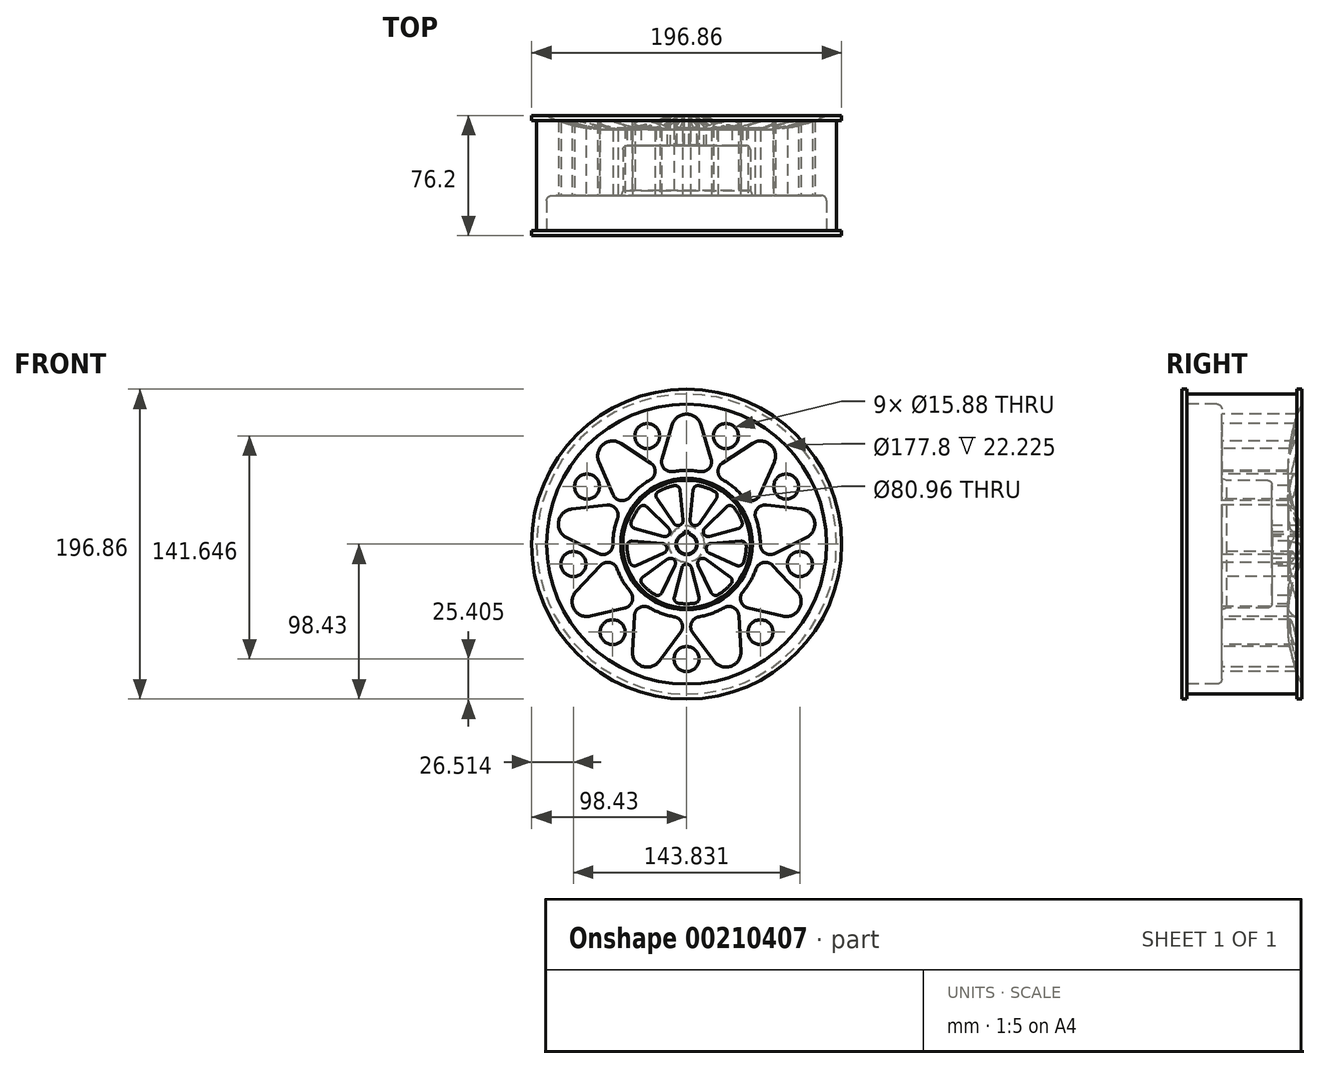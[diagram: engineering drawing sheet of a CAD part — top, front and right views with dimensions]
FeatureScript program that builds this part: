
annotation { "Feature Type Name" : "Feature", "Feature Type Description" : "" }
export const myFeature = defineFeature(function(context is Context, id is Id, definition is map)
    precondition{}
    {
        {
            var Q0;
            Q0=qCreatedBy(makeId("Right.planeOp"),FACE);
            var sketch = newSketch(context, id + "F0", { "sketchPlane" : qUnion([Q0])});
            skLineSegment(sketch, "E0.bottom", {"start": v(-34.93, 95.25) * mm, "end": v(34.92, 95.25) * mm});
            skLineSegment(sketch, "E0.top", {"start": v(19.05, 6.35) * mm, "end": v(38.1, 6.35) * mm});
            skLineSegment(sketch, "E1", {"start": v(38.1, 98.43) * mm, "end": v(34.92, 98.43) * mm});
            skLineSegment(sketch, "E2", {"start": v(34.92, 98.43) * mm, "end": v(34.92, 95.25) * mm});
            skLineSegment(sketch, "E3", {"start": v(38.1, 6.35) * mm, "end": v(38.1, 11.43) * mm});
            skLineSegment(sketch, "E4", {"start": v(-38.1, 88.9) * mm, "end": v(-38.1, 98.43) * mm});
            skLineSegment(sketch, "E5", {"start": v(-38.1, 98.43) * mm, "end": v(-34.93, 98.43) * mm});
            skLineSegment(sketch, "E6", {"start": v(-34.93, 98.43) * mm, "end": v(-34.93, 95.25) * mm});
            skLineSegment(sketch, "E7", {"start": v(-79.55, 0) * mm, "end": v(86.59, 0) * mm, "construction": true});
            skLineSegment(sketch, "E8", {"start": v(19.05, 6.35) * mm, "end": v(19.05, 37.94) * mm});
            skLineSegment(sketch, "E9", {"start": v(-15.88, 88.9) * mm, "end": v(-38.1, 88.9) * mm});
            skLineSegment(sketch, "E10", {"start": v(16.51, 40.48) * mm, "end": v(-12.7, 40.48) * mm});
            skLineSegment(sketch, "E11", {"start": v(-12.7, 40.48) * mm, "end": v(-12.7, 85.73) * mm});
            skPoint(sketch, "E12", {"position": v(38.1, 88.9) * mm});
            skPoint(sketch, "E13", {"position": v(38.1, 11.43) * mm});
            skArc(sketch, "E14", {"start": v(38.1, 88.9) * mm, "mid": v(29.22, 50.16) * mm, "end": v(38.1, 11.43) * mm});
            skLineSegment(sketch, "E15.trimOffspring", {"start": v(38.1, 88.9) * mm, "end": v(38.1, 98.43) * mm});
            skPoint(sketch, "E16.visualSharp", {"position": v(19.05, 40.48) * mm});
            skArc(sketch, "E16.filletArc", {"start": v(19.05, 37.94) * mm, "mid": v(18.3, 39.74) * mm, "end": v(16.51, 40.48) * mm});
            skPoint(sketch, "E17.visualSharp", {"position": v(-12.7, 88.9) * mm});
            skArc(sketch, "E17.filletArc", {"start": v(-12.7, 85.73) * mm, "mid": v(-13.63, 87.97) * mm, "end": v(-15.88, 88.9) * mm});
            skSolve(sketch);
        }
        {
            var Q0;
            Q0 = qSketchRegion(id + "F0", true);
            var Q1;
            Q1=sQuery(id+"F0.wireOp",EDGE,"E7");
            revolve(context, id + "F1", {"entities" : qUnion([Q0]), "axis" : qUnion([Q1]), "revolveType" : RevolveType.FULL});
        }
        {
            var Q0;
            Q0=makeQuery(id+"F1.opRevolve","SWEPT_FACE",FACE,{"disambiguationData":[OSD([sQuery(id+"F0.wireOp",EDGE,"E3")])]});
            var sketch = newSketch(context, id + "F2", { "sketchPlane" : qUnion([Q0])});
            skLineSegment(sketch, "E18.bottom", {"start": v(-1.59, 4.76) * mm, "end": v(1.59, 4.76) * mm});
            skLineSegment(sketch, "E18.top", {"start": v(-1.59, 7.94) * mm, "end": v(1.59, 7.94) * mm});
            skLineSegment(sketch, "E18.left", {"start": v(-1.59, 4.76) * mm, "end": v(-1.59, 7.94) * mm});
            skLineSegment(sketch, "E18.right", {"start": v(1.59, 4.76) * mm, "end": v(1.59, 7.94) * mm});
            skLineSegment(sketch, "E19", {"start": v(-1.59, 7.94) * mm, "end": v(1.59, 4.76) * mm, "construction": true});
            skPoint(sketch, "E20", {"position": v(0, 6.35) * mm});
            skSolve(sketch);
        }
        {
            var Q0;
            Q0 = qSketchRegion(id + "F2", true);
            extrude(context, id + "F3", {"entities" : qUnion([Q0]), "operationType" : NewBodyOperationType.REMOVE, "endBound" : BoundingType.THROUGH_ALL, "oppositeDirection" : true, "depth" : 25.4 * mm});
        }
        {
            var Q0;
            Q0=makeQuery(id+"F1.opRevolve","SWEPT_FACE",FACE,{"disambiguationData":[OSD([sQuery(id+"F0.wireOp",EDGE,"E11")])]});
            var sketch = newSketch(context, id + "F4", { "sketchPlane" : qUnion([Q0])});
            skArc(sketch, "E21", {"start": v(8.39, 46.07) * mm, "mid": v(0, 46.83) * mm, "end": v(-8.39, 46.07) * mm});
            skCircle(sketch, "E22", {"center": v(0, 0) * mm, "radius": 82.55 * mm, "construction": true});
            skArc(sketch, "E23", {"start": v(9.12, 75.76) * mm, "mid": v(0, 82.55) * mm, "end": v(-9.12, 75.76) * mm});
            skArc(sketch, "E24", {"start": v(8.39, 46.07) * mm, "mid": v(14.26, 48.09) * mm, "end": v(15.6, 54.15) * mm});
            skArc(sketch, "E25", {"start": v(-15.6, 54.15) * mm, "mid": v(-14.26, 48.09) * mm, "end": v(-8.39, 46.07) * mm});
            skLineSegment(sketch, "E26", {"start": v(-9.53, 52.32) * mm, "end": v(9.52, 52.32) * mm, "construction": true});
            skLineSegment(sketch, "E27", {"start": v(0, 0) * mm, "end": v(0, 105.17) * mm, "construction": true});
            skLineSegment(sketch, "E28", {"start": v(9.12, 75.76) * mm, "end": v(15.6, 54.15) * mm});
            skLineSegment(sketch, "E29", {"start": v(-9.12, 75.76) * mm, "end": v(-15.6, 54.15) * mm});
            skArc(sketch, "E30.1.0", {"start": v(-41.7, 63.9) * mm, "mid": v(-53.06, 63.24) * mm, "end": v(-55.69, 52.17) * mm});
            skLineSegment(sketch, "E30.1.1", {"start": v(-55.69, 52.17) * mm, "end": v(-46.76, 31.45) * mm});
            skArc(sketch, "E30.1.2", {"start": v(-46.76, 31.45) * mm, "mid": v(-41.83, 27.67) * mm, "end": v(-36.04, 29.9) * mm});
            skArc(sketch, "E30.1.3", {"start": v(-23.2, 40.69) * mm, "mid": v(-30.1, 35.87) * mm, "end": v(-36.04, 29.9) * mm});
            skArc(sketch, "E30.1.4", {"start": v(-23.2, 40.69) * mm, "mid": v(-19.99, 46) * mm, "end": v(-22.85, 51.51) * mm});
            skLineSegment(sketch, "E30.1.5", {"start": v(-41.7, 63.9) * mm, "end": v(-22.85, 51.51) * mm});
            skArc(sketch, "E30.2.0", {"start": v(-73.03, 22.14) * mm, "mid": v(-81.3, 14.33) * mm, "end": v(-76.2, 4.17) * mm});
            skLineSegment(sketch, "E30.2.1", {"start": v(-76.2, 4.17) * mm, "end": v(-56.03, -5.97) * mm});
            skArc(sketch, "E30.2.2", {"start": v(-56.03, -5.97) * mm, "mid": v(-49.83, -5.7) * mm, "end": v(-46.83, -0.26) * mm});
            skArc(sketch, "E30.2.3", {"start": v(-43.92, 16.26) * mm, "mid": v(-46.12, 8.13) * mm, "end": v(-46.83, -0.26) * mm});
            skArc(sketch, "E30.2.4", {"start": v(-43.92, 16.26) * mm, "mid": v(-44.88, 22.4) * mm, "end": v(-50.61, 24.77) * mm});
            skLineSegment(sketch, "E30.2.5", {"start": v(-73.03, 22.14) * mm, "end": v(-50.61, 24.77) * mm});
            skArc(sketch, "E30.3.0", {"start": v(-70.17, -29.98) * mm, "mid": v(-71.5, -41.27) * mm, "end": v(-61.05, -45.78) * mm});
            skLineSegment(sketch, "E30.3.1", {"start": v(-61.05, -45.78) * mm, "end": v(-39.09, -40.59) * mm});
            skArc(sketch, "E30.3.2", {"start": v(-39.09, -40.59) * mm, "mid": v(-34.52, -36.4) * mm, "end": v(-35.7, -30.3) * mm});
            skArc(sketch, "E30.3.3", {"start": v(-44.1, -15.77) * mm, "mid": v(-40.56, -23.42) * mm, "end": v(-35.7, -30.3) * mm});
            skArc(sketch, "E30.3.4", {"start": v(-44.1, -15.77) * mm, "mid": v(-48.77, -11.7) * mm, "end": v(-54.7, -13.56) * mm});
            skLineSegment(sketch, "E30.3.5", {"start": v(-70.17, -29.98) * mm, "end": v(-54.7, -13.56) * mm});
            skArc(sketch, "E30.4.0", {"start": v(-34.49, -68.07) * mm, "mid": v(-28.23, -77.57) * mm, "end": v(-17.34, -74.31) * mm});
            skLineSegment(sketch, "E30.4.1", {"start": v(-17.34, -74.31) * mm, "end": v(-3.85, -56.22) * mm});
            skArc(sketch, "E30.4.2", {"start": v(-3.85, -56.22) * mm, "mid": v(-3.05, -50.06) * mm, "end": v(-7.88, -46.16) * mm});
            skArc(sketch, "E30.4.3", {"start": v(-23.64, -40.43) * mm, "mid": v(-16.02, -44) * mm, "end": v(-7.88, -46.16) * mm});
            skArc(sketch, "E30.4.4", {"start": v(-23.64, -40.43) * mm, "mid": v(-29.85, -40.31) * mm, "end": v(-33.18, -45.54) * mm});
            skLineSegment(sketch, "E30.4.5", {"start": v(-34.49, -68.07) * mm, "end": v(-33.18, -45.54) * mm});
            skArc(sketch, "E30.5.0", {"start": v(17.34, -74.31) * mm, "mid": v(28.23, -77.57) * mm, "end": v(34.49, -68.07) * mm});
            skLineSegment(sketch, "E30.5.1", {"start": v(34.49, -68.07) * mm, "end": v(33.18, -45.54) * mm});
            skArc(sketch, "E30.5.2", {"start": v(33.18, -45.54) * mm, "mid": v(29.85, -40.31) * mm, "end": v(23.64, -40.43) * mm});
            skArc(sketch, "E30.5.3", {"start": v(7.88, -46.16) * mm, "mid": v(16.02, -44) * mm, "end": v(23.64, -40.43) * mm});
            skArc(sketch, "E30.5.4", {"start": v(7.88, -46.16) * mm, "mid": v(3.05, -50.06) * mm, "end": v(3.85, -56.22) * mm});
            skLineSegment(sketch, "E30.5.5", {"start": v(17.34, -74.31) * mm, "end": v(3.85, -56.22) * mm});
            skArc(sketch, "E30.6.0", {"start": v(61.05, -45.78) * mm, "mid": v(71.5, -41.28) * mm, "end": v(70.17, -29.98) * mm});
            skLineSegment(sketch, "E30.6.1", {"start": v(70.17, -29.98) * mm, "end": v(54.7, -13.56) * mm});
            skArc(sketch, "E30.6.2", {"start": v(54.7, -13.56) * mm, "mid": v(48.77, -11.7) * mm, "end": v(44.1, -15.77) * mm});
            skArc(sketch, "E30.6.3", {"start": v(35.7, -30.3) * mm, "mid": v(40.56, -23.42) * mm, "end": v(44.1, -15.77) * mm});
            skArc(sketch, "E30.6.4", {"start": v(35.7, -30.3) * mm, "mid": v(34.52, -36.4) * mm, "end": v(39.09, -40.59) * mm});
            skLineSegment(sketch, "E30.6.5", {"start": v(61.05, -45.78) * mm, "end": v(39.09, -40.59) * mm});
            skArc(sketch, "E30.7.0", {"start": v(76.2, 4.17) * mm, "mid": v(81.3, 14.33) * mm, "end": v(73.03, 22.14) * mm});
            skLineSegment(sketch, "E30.7.1", {"start": v(73.03, 22.14) * mm, "end": v(50.61, 24.77) * mm});
            skArc(sketch, "E30.7.2", {"start": v(50.61, 24.77) * mm, "mid": v(44.88, 22.4) * mm, "end": v(43.92, 16.26) * mm});
            skArc(sketch, "E30.7.3", {"start": v(46.83, -0.26) * mm, "mid": v(46.12, 8.13) * mm, "end": v(43.92, 16.26) * mm});
            skArc(sketch, "E30.7.4", {"start": v(46.83, -0.26) * mm, "mid": v(49.83, -5.7) * mm, "end": v(56.03, -5.97) * mm});
            skLineSegment(sketch, "E30.7.5", {"start": v(76.2, 4.17) * mm, "end": v(56.03, -5.97) * mm});
            skArc(sketch, "E30.8.0", {"start": v(55.69, 52.17) * mm, "mid": v(53.06, 63.24) * mm, "end": v(41.7, 63.9) * mm});
            skLineSegment(sketch, "E30.8.1", {"start": v(41.7, 63.9) * mm, "end": v(22.85, 51.51) * mm});
            skArc(sketch, "E30.8.2", {"start": v(22.85, 51.51) * mm, "mid": v(19.99, 46) * mm, "end": v(23.2, 40.69) * mm});
            skArc(sketch, "E30.8.3", {"start": v(36.04, 29.9) * mm, "mid": v(30.1, 35.87) * mm, "end": v(23.2, 40.69) * mm});
            skArc(sketch, "E30.8.4", {"start": v(36.04, 29.9) * mm, "mid": v(41.83, 27.67) * mm, "end": v(46.76, 31.45) * mm});
            skLineSegment(sketch, "E30.8.5", {"start": v(55.69, 52.17) * mm, "end": v(46.76, 31.45) * mm});
            skSolve(sketch);
        }
        {
            var Q0;
            Q0 = qSketchRegion(id + "F4", true);
            extrude(context, id + "F5", {"entities" : qUnion([Q0]), "operationType" : NewBodyOperationType.REMOVE, "endBound" : BoundingType.UP_TO_NEXT, "oppositeDirection" : true, "depth" : 25.4 * mm});
        }
        {
            var Q0;
            Q0=qCreatedBy(makeId("Front.planeOp"),FACE);
            var sketch = newSketch(context, id + "F6", { "sketchPlane" : qUnion([Q0])});
            skCircle(sketch, "E31", {"center": v(0, 0) * mm, "radius": 73.03 * mm, "construction": true});
            skCircle(sketch, "E32", {"center": v(0, -73.03) * mm, "radius": 7.94 * mm});
            skCircle(sketch, "E33.1.0", {"center": v(46.94, -55.94) * mm, "radius": 7.94 * mm});
            skCircle(sketch, "E33.2.0", {"center": v(71.92, -12.68) * mm, "radius": 7.94 * mm});
            skCircle(sketch, "E33.3.0", {"center": v(63.24, 36.51) * mm, "radius": 7.94 * mm});
            skCircle(sketch, "E33.4.0", {"center": v(24.98, 68.62) * mm, "radius": 7.94 * mm});
            skCircle(sketch, "E33.5.0", {"center": v(-24.98, 68.62) * mm, "radius": 7.94 * mm});
            skCircle(sketch, "E33.6.0", {"center": v(-63.24, 36.51) * mm, "radius": 7.94 * mm});
            skCircle(sketch, "E33.7.0", {"center": v(-71.92, -12.68) * mm, "radius": 7.94 * mm});
            skCircle(sketch, "E34.1.8.0", {"center": v(-46.94, -55.94) * mm, "radius": 7.94 * mm});
            skSolve(sketch);
        }
        {
            var Q0;
            Q0 = qSketchRegion(id + "F6", true);
            extrude(context, id + "F7", {"entities" : qUnion([Q0]), "operationType" : NewBodyOperationType.REMOVE, "endBound" : BoundingType.SYMMETRIC, "oppositeDirection" : true, "depth" : 101.6 * mm});
        }
        {
            var Q0;
            Q0=makeQuery(id+"F1.opRevolve","SWEPT_EDGE",EDGE,{"disambiguationData":[OSD([sQuery(id+"F0.wireOp",EDGE,"E10"),sQuery(id+"F0.wireOp",EDGE,"E11")])]});
            chamfer(context, id + "F8", {"entities" : qUnion([Q0]), "chamferType" : ChamferType.TWO_OFFSETS, "width1" : 3.17 * mm, "oppositeDirection" : false, "width2" : 1.27 * mm, "tangentPropagation" : true});
        }
        {
            var Q0;
            Q0=makeQuery(id+"F1.opRevolve","SWEPT_EDGE",EDGE,{"disambiguationData":[OSD([sQuery(id+"F0.wireOp",EDGE,"E0.top"),sQuery(id+"F0.wireOp",EDGE,"E8")])]});
            chamfer(context, id + "F9", {"entities" : qUnion([Q0]), "width" : 0.38 * mm, "tangentPropagation" : true});
        }
        {
            var Q0;
            Q0=makeQuery(id+"F1.opRevolve","SWEPT_FACE",FACE,{"disambiguationData":[OSD([sQuery(id+"F0.wireOp",EDGE,"E8")])]});
            var sketch = newSketch(context, id + "F10", { "sketchPlane" : qUnion([Q0])});
            skCircle(sketch, "E35.0", {"center": v(0, 0) * mm, "radius": 12.7 * mm, "construction": true});
            skArc(sketch, "E36", {"start": v(3.08, -15.09) * mm, "mid": v(0, -12.7) * mm, "end": v(-3.08, -15.09) * mm});
            skArc(sketch, "E37", {"start": v(5.2, -37.58) * mm, "mid": v(7.4, -36.2) * mm, "end": v(7.84, -33.65) * mm});
            skArc(sketch, "E38", {"start": v(-7.84, -33.65) * mm, "mid": v(-7.4, -36.2) * mm, "end": v(-5.2, -37.58) * mm});
            skLineSegment(sketch, "E39", {"start": v(4.76, -34.44) * mm, "end": v(-4.76, -34.44) * mm, "construction": true});
            skPoint(sketch, "E40", {"position": v(0, -34.44) * mm});
            skLineSegment(sketch, "E41", {"start": v(-3.08, -15.09) * mm, "end": v(-7.84, -33.65) * mm});
            skLineSegment(sketch, "E42", {"start": v(3.08, -15.09) * mm, "end": v(7.84, -33.65) * mm});
            skArc(sketch, "E43.0", {"start": v(-5.2, -37.58) * mm, "mid": v(0, -37.94) * mm, "end": v(5.2, -37.58) * mm});
            skArc(sketch, "E44.1.0", {"start": v(12.05, -9.58) * mm, "mid": v(8.16, -9.73) * mm, "end": v(7.34, -13.53) * mm});
            skLineSegment(sketch, "E44.1.1", {"start": v(7.34, -13.53) * mm, "end": v(15.63, -30.82) * mm});
            skArc(sketch, "E44.1.2", {"start": v(15.63, -30.82) * mm, "mid": v(17.6, -32.5) * mm, "end": v(20.18, -32.13) * mm});
            skArc(sketch, "E44.1.3", {"start": v(20.18, -32.13) * mm, "mid": v(24.39, -29.06) * mm, "end": v(28.14, -25.45) * mm});
            skArc(sketch, "E44.1.4", {"start": v(28.14, -25.45) * mm, "mid": v(28.94, -22.98) * mm, "end": v(27.63, -20.74) * mm});
            skLineSegment(sketch, "E44.1.5", {"start": v(12.05, -9.58) * mm, "end": v(27.63, -20.74) * mm});
            skArc(sketch, "E44.2.0", {"start": v(15.4, 0.4) * mm, "mid": v(12.5, -2.2) * mm, "end": v(14.32, -5.65) * mm});
            skLineSegment(sketch, "E44.2.1", {"start": v(14.32, -5.65) * mm, "end": v(31.78, -13.56) * mm});
            skArc(sketch, "E44.2.2", {"start": v(31.78, -13.56) * mm, "mid": v(34.37, -13.57) * mm, "end": v(36.11, -11.64) * mm});
            skArc(sketch, "E44.2.3", {"start": v(36.11, -11.64) * mm, "mid": v(37.36, -6.59) * mm, "end": v(37.92, -1.4) * mm});
            skArc(sketch, "E44.2.4", {"start": v(37.92, -1.4) * mm, "mid": v(36.94, 1) * mm, "end": v(34.5, 1.88) * mm});
            skLineSegment(sketch, "E44.2.5", {"start": v(15.4, 0.4) * mm, "end": v(34.5, 1.88) * mm});
            skArc(sketch, "E44.3.0", {"start": v(11.53, 10.2) * mm, "mid": v(11, 6.35) * mm, "end": v(14.6, 4.88) * mm});
            skLineSegment(sketch, "E44.3.1", {"start": v(14.6, 4.88) * mm, "end": v(33.06, 10.04) * mm});
            skArc(sketch, "E44.3.2", {"start": v(33.06, 10.04) * mm, "mid": v(35.06, 11.7) * mm, "end": v(35.15, 14.3) * mm});
            skArc(sketch, "E44.3.3", {"start": v(35.15, 14.3) * mm, "mid": v(32.86, 18.97) * mm, "end": v(29.95, 23.3) * mm});
            skArc(sketch, "E44.3.4", {"start": v(29.95, 23.3) * mm, "mid": v(27.66, 24.51) * mm, "end": v(25.22, 23.61) * mm});
            skLineSegment(sketch, "E44.3.5", {"start": v(11.53, 10.2) * mm, "end": v(25.22, 23.61) * mm});
            skArc(sketch, "E44.4.0", {"start": v(2.27, 15.23) * mm, "mid": v(4.34, 11.93) * mm, "end": v(8.05, 13.12) * mm});
            skLineSegment(sketch, "E44.4.1", {"start": v(8.05, 13.12) * mm, "end": v(18.87, 28.94) * mm});
            skArc(sketch, "E44.4.2", {"start": v(18.87, 28.94) * mm, "mid": v(19.34, 31.5) * mm, "end": v(17.74, 33.54) * mm});
            skArc(sketch, "E44.4.3", {"start": v(17.74, 33.54) * mm, "mid": v(12.98, 35.65) * mm, "end": v(7.97, 37.1) * mm});
            skArc(sketch, "E44.4.4", {"start": v(7.97, 37.1) * mm, "mid": v(5.43, 36.55) * mm, "end": v(4.14, 34.3) * mm});
            skLineSegment(sketch, "E44.4.5", {"start": v(2.27, 15.23) * mm, "end": v(4.14, 34.3) * mm});
            skArc(sketch, "E44.5.0", {"start": v(-8.05, 13.12) * mm, "mid": v(-4.34, 11.93) * mm, "end": v(-2.27, 15.23) * mm});
            skLineSegment(sketch, "E44.5.1", {"start": v(-2.27, 15.23) * mm, "end": v(-4.14, 34.3) * mm});
            skArc(sketch, "E44.5.2", {"start": v(-4.14, 34.3) * mm, "mid": v(-5.43, 36.55) * mm, "end": v(-7.97, 37.1) * mm});
            skArc(sketch, "E44.5.3", {"start": v(-7.97, 37.1) * mm, "mid": v(-12.98, 35.65) * mm, "end": v(-17.74, 33.54) * mm});
            skArc(sketch, "E44.5.4", {"start": v(-17.74, 33.54) * mm, "mid": v(-19.34, 31.5) * mm, "end": v(-18.87, 28.94) * mm});
            skLineSegment(sketch, "E44.5.5", {"start": v(-8.05, 13.12) * mm, "end": v(-18.87, 28.94) * mm});
            skArc(sketch, "E44.6.0", {"start": v(-14.6, 4.88) * mm, "mid": v(-11, 6.35) * mm, "end": v(-11.53, 10.2) * mm});
            skLineSegment(sketch, "E44.6.1", {"start": v(-11.53, 10.2) * mm, "end": v(-25.22, 23.61) * mm});
            skArc(sketch, "E44.6.2", {"start": v(-25.22, 23.61) * mm, "mid": v(-27.66, 24.51) * mm, "end": v(-29.95, 23.3) * mm});
            skArc(sketch, "E44.6.3", {"start": v(-29.95, 23.3) * mm, "mid": v(-32.86, 18.97) * mm, "end": v(-35.15, 14.3) * mm});
            skArc(sketch, "E44.6.4", {"start": v(-35.15, 14.3) * mm, "mid": v(-35.06, 11.7) * mm, "end": v(-33.06, 10.04) * mm});
            skLineSegment(sketch, "E44.6.5", {"start": v(-14.6, 4.88) * mm, "end": v(-33.06, 10.04) * mm});
            skArc(sketch, "E44.7.0", {"start": v(-14.32, -5.65) * mm, "mid": v(-12.5, -2.2) * mm, "end": v(-15.4, 0.4) * mm});
            skLineSegment(sketch, "E44.7.1", {"start": v(-15.4, 0.4) * mm, "end": v(-34.5, 1.88) * mm});
            skArc(sketch, "E44.7.2", {"start": v(-34.5, 1.88) * mm, "mid": v(-36.94, 1) * mm, "end": v(-37.92, -1.4) * mm});
            skArc(sketch, "E44.7.3", {"start": v(-37.92, -1.4) * mm, "mid": v(-37.36, -6.59) * mm, "end": v(-36.11, -11.64) * mm});
            skArc(sketch, "E44.7.4", {"start": v(-36.11, -11.64) * mm, "mid": v(-34.37, -13.57) * mm, "end": v(-31.78, -13.56) * mm});
            skLineSegment(sketch, "E44.7.5", {"start": v(-14.32, -5.65) * mm, "end": v(-31.78, -13.56) * mm});
            skArc(sketch, "E44.8.0", {"start": v(-7.34, -13.53) * mm, "mid": v(-8.16, -9.73) * mm, "end": v(-12.05, -9.58) * mm});
            skLineSegment(sketch, "E44.8.1", {"start": v(-12.05, -9.58) * mm, "end": v(-27.63, -20.74) * mm});
            skArc(sketch, "E44.8.2", {"start": v(-27.63, -20.74) * mm, "mid": v(-28.94, -22.98) * mm, "end": v(-28.14, -25.45) * mm});
            skArc(sketch, "E44.8.3", {"start": v(-28.14, -25.45) * mm, "mid": v(-24.39, -29.06) * mm, "end": v(-20.18, -32.13) * mm});
            skArc(sketch, "E44.8.4", {"start": v(-20.18, -32.13) * mm, "mid": v(-17.6, -32.5) * mm, "end": v(-15.63, -30.82) * mm});
            skLineSegment(sketch, "E44.8.5", {"start": v(-7.34, -13.53) * mm, "end": v(-15.63, -30.82) * mm});
            skSolve(sketch);
        }
        {
            var Q0;
            Q0 = qSketchRegion(id + "F10", true);
            extrude(context, id + "F11", {"entities" : qUnion([Q0]), "operationType" : NewBodyOperationType.REMOVE, "endBound" : BoundingType.UP_TO_NEXT, "oppositeDirection" : true, "depth" : 25.4 * mm});
        }
    });
